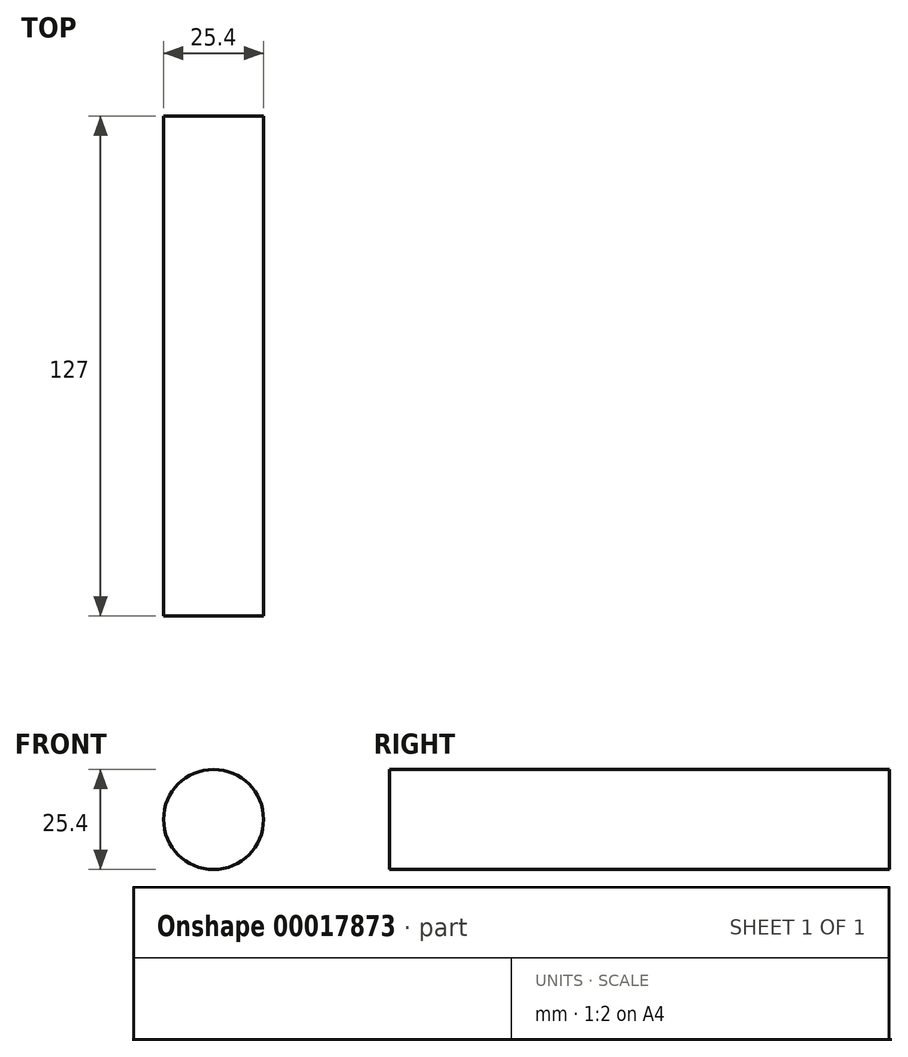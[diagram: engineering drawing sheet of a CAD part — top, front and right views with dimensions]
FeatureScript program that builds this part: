
annotation { "Feature Type Name" : "Feature", "Feature Type Description" : "" }
export const myFeature = defineFeature(function(context is Context, id is Id, definition is map)
    precondition{}
    {
        {
            var Q0;
            Q0=qCreatedBy(makeId("Front.planeOp"),FACE);
            var sketch = newSketch(context, id + "F0", { "sketchPlane" : qUnion([Q0])});
            skCircle(sketch, "E0", {"center": v(0, 0) * mm, "radius": 12.7 * mm});
            skSolve(sketch);
        }
        {
            var Q0;
            Q0 = qSketchRegion(id + "F0", true);
            extrude(context, id + "F1", {"entities" : qUnion([Q0]), "depth" : 127 * mm});
        }
    });
